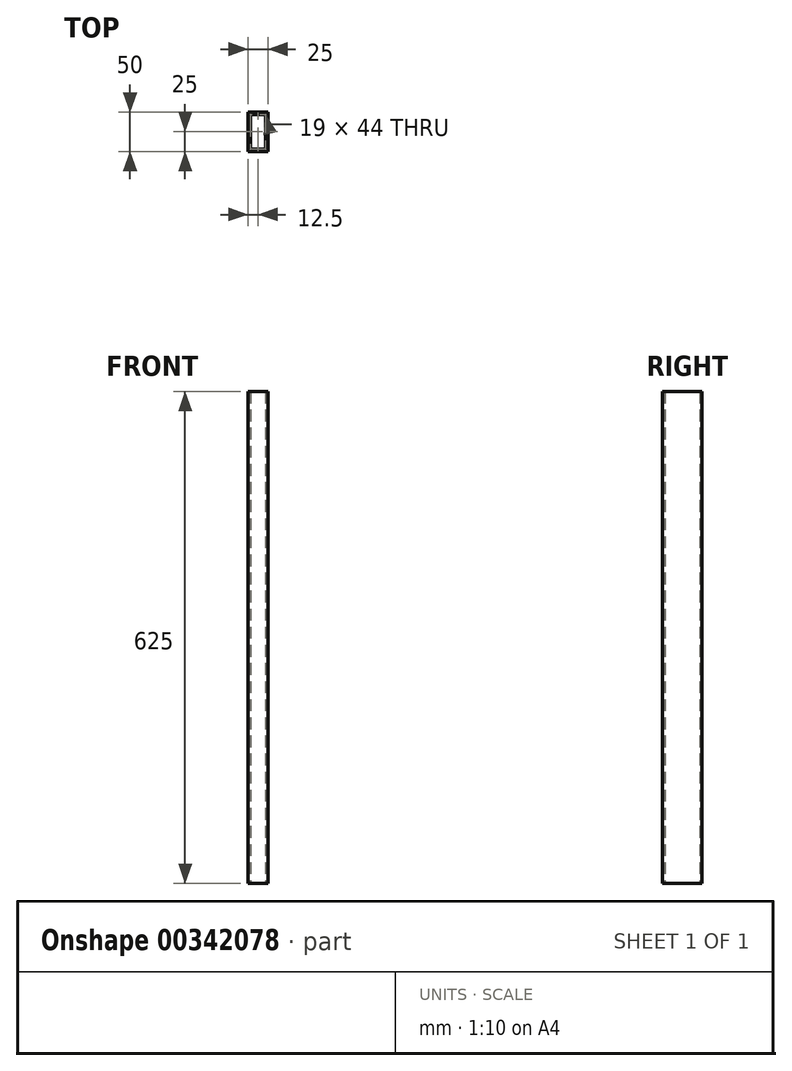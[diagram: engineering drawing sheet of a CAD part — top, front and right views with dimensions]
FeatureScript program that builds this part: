
annotation { "Feature Type Name" : "Feature", "Feature Type Description" : "" }
export const myFeature = defineFeature(function(context is Context, id is Id, definition is map)
    precondition{}
    {
        {
            var Q0;
            Q0=qCreatedBy(makeId("Top.planeOp"),FACE);
            var sketch = newSketch(context, id + "F0", { "sketchPlane" : qUnion([Q0])});
            skLineSegment(sketch, "E0.bottom", {"start": v(-12.5, -25) * mm, "end": v(12.5, -25) * mm});
            skLineSegment(sketch, "E0.top", {"start": v(-12.5, 25) * mm, "end": v(12.5, 25) * mm});
            skLineSegment(sketch, "E0.left", {"start": v(-12.5, -25) * mm, "end": v(-12.5, 25) * mm});
            skLineSegment(sketch, "E0.right", {"start": v(12.5, -25) * mm, "end": v(12.5, 25) * mm});
            skPoint(sketch, "E0.middle", {"position": v(0, 0) * mm});
            skLineSegment(sketch, "E1.bottom", {"start": v(-9.5, 22) * mm, "end": v(9.5, 22) * mm});
            skLineSegment(sketch, "E1.top", {"start": v(-9.5, -22) * mm, "end": v(9.5, -22) * mm});
            skLineSegment(sketch, "E1.left", {"start": v(-9.5, 22) * mm, "end": v(-9.5, -22) * mm});
            skLineSegment(sketch, "E1.right", {"start": v(9.5, 22) * mm, "end": v(9.5, -22) * mm});
            skSolve(sketch);
        }
        {
            var Q0;
            Q0=makeQuery(id+"F0.imprint","IMPRINT",FACE,{"disambiguationData":[TD([[makeQuery(id+"F0.imprint","IMPRINT",EDGE,{"derivedFrom":sQuery(id+"F0.wireOp",EDGE,"E0.bottom")}),1.0]])]});
            extrude(context, id + "F1", {"entities" : qUnion([Q0]), "endBound" : BoundingType.SYMMETRIC, "depth" : 625 * mm});
        }
    });
